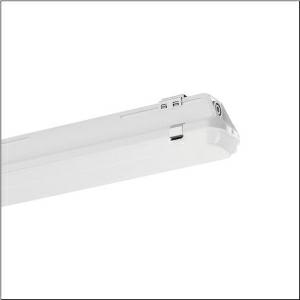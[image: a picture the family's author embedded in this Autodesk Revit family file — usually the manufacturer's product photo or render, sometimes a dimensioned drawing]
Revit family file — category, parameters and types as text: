
# Revit family: monsun_r__11_51fp20dp460l_ba2d
name_source: partatom
category: Lighting Fixtures
units: mm (PartAtom-declared; Revit-internal decimal feet)

## family parameters
Cut with Voids When Loaded = No
Host = Face
Light Source = No
Part Type = Normal
Room Calculation Point = No
Round Connector Dimension = Use Diameter
Shared = No

## types (1)
- --- (1 x LED, 5450 lm, 31.5 W, 4000K)
    Apparent Load = 32 VA
    CIE Flux Codes = 45 75 93 94 100
    Color Rendering = 80
    Color Temperature = 4000K
    Default Elevation = 1800 mm
    Description = Monsun® 11, damp-proof luminaire, chain hanger, primary optical cover: enclosure, of PC, light emission: direct distribution, primary light characteristic: symmetric, installation type: suspended mounting, surface-mounted, horizontal mounting, vertical mounting, LED, rated luminous flux: 5.450lm, luminous efficacy: 173lm/W, light colour: 840, colour temperature: 4000K, control gear: DALI 2, with terminal, 5-pole, max. 2.5mm², mains connection: 220..240V, AC, 50/60Hz, rated input power: 32W, luminaire housing, of glass-fibre reinforced polyester, uncoated, bright grey, incl. chain hanger, length: 1.590mm, width: 90mm, height: 88mm, clip for enclosure, of stainless steel (V2A), ceiling mounting element, of stainless steel (V2A), chain hanger, of stainless steel (V2A), protection rating (complete): IP66, insulation class (complete): insulation class I (protective earthing), certification: CE, ENEC, VDE, UKCA, protection symbol: D, impact resistance: IK08, permissible operating ambient temperature: -35..+40°C, standard: EN 50419, EN 60598-2-1, corresponds to IFS (International Featured Standards) requirements for safety and quality in the food industry, for indoor or canopied outdoor use, no direct snow, no direct sun, no direct rain, LABS conformity tested according to VDMA 24364:2018-05, contact your sales advisor before using the luminaires in applications with unclear chemical exposure, large temperature fluctuations or condensation-forming humidity, packaging unit: 1 piece
    Height = 89 mm
    Lamp = 1 x LED
    Lamp Light Flux = 5450 lm
    Lamp Power = 31.5 W
    Lamp count = 1
    Length = 1590 mm
    Luminous efficacy = 173 lm/W
    Manufacturer = Siteco
    ModVariant = No
    Model = 51FP20DP460L
    Mounting Place = Ceiling
    Mounting Type = Surface mounted
    Number of Poles = 1
    OnlyDefault = Yes
    Power Factor = 1
    Product Name = Monsun® 11
    Product group = damp-proof luminaire
    ProductGroupID = 300
    Protection Class = Protection class I
    Protection Degree = IP 66
    RLX_Detail_Level = 1
    RLX_Emergency_Light_Flux = 0 lm
    RLX_Emergency_Type = 0
    RLX_Emergency_Type_DB = No
    RlxData = <blob elided: 92285 chars, md5=2739d35c>
    Socket = socket
    Standby Power = 0 W
    System Light Flux = 5450 lm
    System Power = 32 W
    Type Comments = factory setting: luminous flux: 100 % | dim-lin: 254 | 219 mA
    Type Image = l_1349237.jpg
    URL = http://relux.com
    VarID = @adj_018312
    Voltage = 0 V
    Weight = 0.00 kg
    Width = 90 mm

## geometry (parser evidence)
native form markers: Blend x4, Sweep x16
no freeform markers — native parametric forms only
